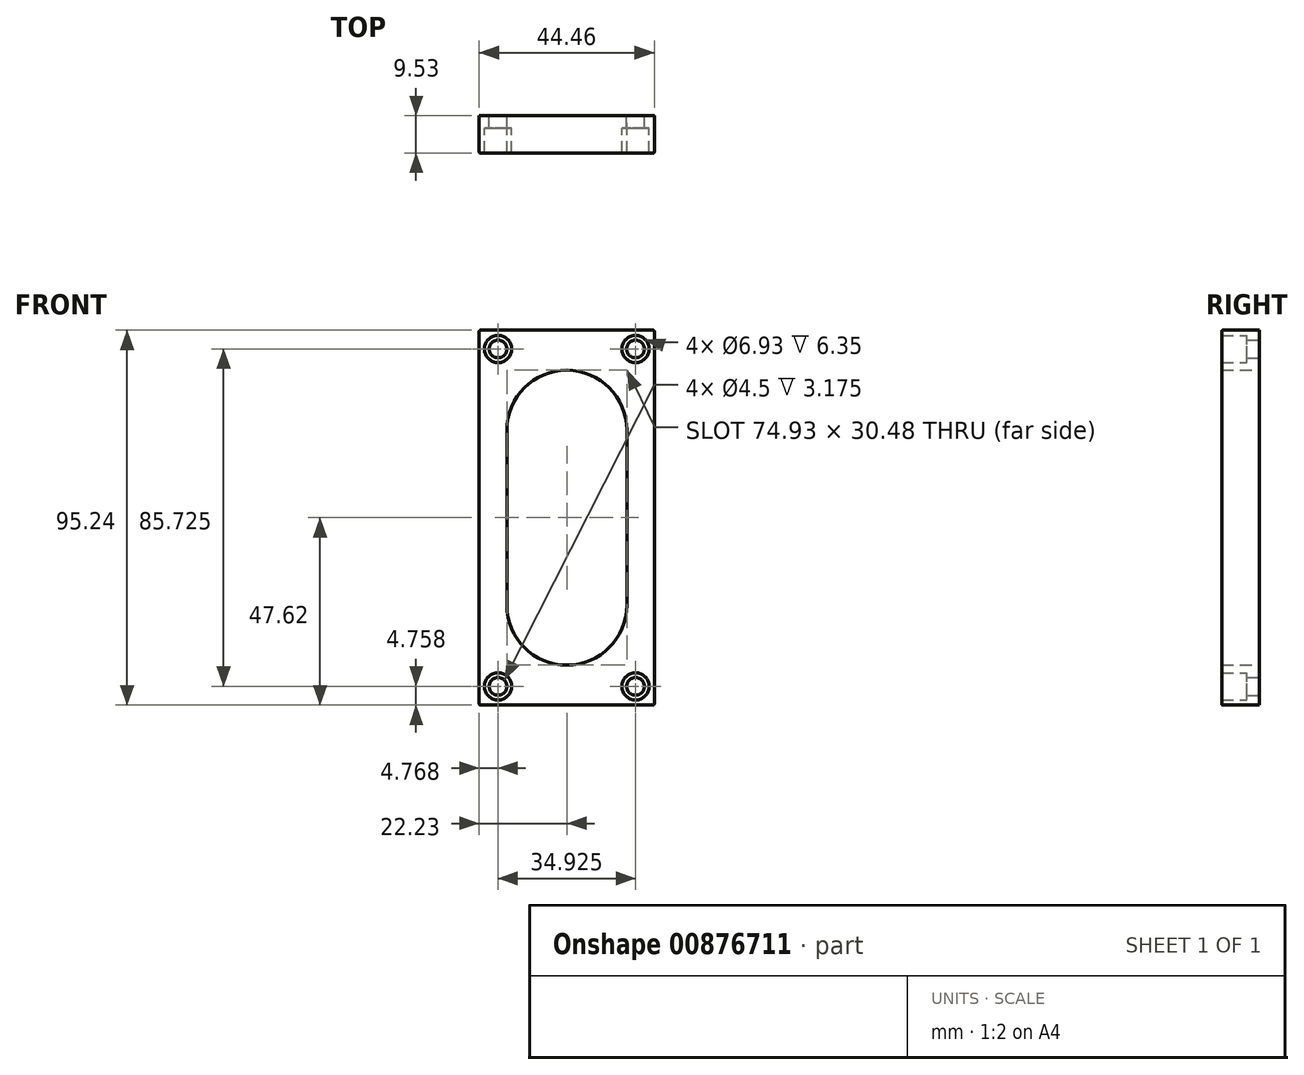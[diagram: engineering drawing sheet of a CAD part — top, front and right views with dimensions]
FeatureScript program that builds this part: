
annotation { "Feature Type Name" : "Feature", "Feature Type Description" : "" }
export const myFeature = defineFeature(function(context is Context, id is Id, definition is map)
    precondition{}
    {
        {
            var Q0;
            Q0=qCreatedBy(makeId("Front.planeOp"),FACE);
            var sketch = newSketch(context, id + "F0", { "sketchPlane" : qUnion([Q0])});
            skLineSegment(sketch, "E0.bottom", {"start": v(-22.23, 47.62) * mm, "end": v(22.23, 47.63) * mm});
            skLineSegment(sketch, "E0.top", {"start": v(-22.23, -47.63) * mm, "end": v(22.23, -47.62) * mm});
            skLineSegment(sketch, "E0.left", {"start": v(-22.23, 47.62) * mm, "end": v(-22.23, -47.63) * mm});
            skLineSegment(sketch, "E0.right", {"start": v(22.23, 47.63) * mm, "end": v(22.23, -47.62) * mm});
            skPoint(sketch, "E0.middle", {"position": v(0, 0) * mm});
            skPoint(sketch, "E1", {"position": v(17.46, 42.86) * mm});
            skPoint(sketch, "E2", {"position": v(-17.46, 42.86) * mm});
            skPoint(sketch, "E3", {"position": v(-17.46, -42.86) * mm});
            skPoint(sketch, "E4", {"position": v(17.46, -42.86) * mm});
            skCircle(sketch, "E5", {"center": v(-17.46, 42.86) * mm, "radius": 2.25 * mm});
            skCircle(sketch, "E6", {"center": v(17.46, 42.86) * mm, "radius": 2.25 * mm});
            skCircle(sketch, "E7", {"center": v(-17.46, -42.86) * mm, "radius": 2.25 * mm});
            skCircle(sketch, "E8", {"center": v(17.46, -42.86) * mm, "radius": 2.25 * mm});
            skPoint(sketch, "E9", {"position": v(0, 22.22) * mm});
            skPoint(sketch, "E10", {"position": v(0, -22.23) * mm});
            skArc(sketch, "E11", {"start": v(15.24, 22.22) * mm, "mid": v(0, 37.46) * mm, "end": v(-15.24, 22.22) * mm});
            skArc(sketch, "E12", {"start": v(15.24, -22.23) * mm, "mid": v(0, -37.47) * mm, "end": v(-15.24, -22.23) * mm});
            skLineSegment(sketch, "E13", {"start": v(-15.24, 22.23) * mm, "end": v(-15.24, -22.23) * mm});
            skLineSegment(sketch, "E14", {"start": v(15.24, 22.23) * mm, "end": v(15.24, -22.23) * mm});
            skCircle(sketch, "E15", {"center": v(17.46, 42.86) * mm, "radius": 3.47 * mm});
            skCircle(sketch, "E16", {"center": v(-17.46, 42.86) * mm, "radius": 3.47 * mm});
            skCircle(sketch, "E17", {"center": v(-17.46, -42.86) * mm, "radius": 3.47 * mm});
            skCircle(sketch, "E18", {"center": v(17.46, -42.86) * mm, "radius": 3.47 * mm});
            skSolve(sketch);
        }
        {
            var Q0;
            Q0=makeQuery(id+"F0.imprint","IMPRINT",FACE,{"disambiguationData":[TD([[makeQuery(id+"F0.imprint","IMPRINT",EDGE,{"derivedFrom":sQuery(id+"F0.wireOp",EDGE,"E0.bottom")}),-1.0]])]});
            extrude(context, id + "F1", {"entities" : qUnion([Q0]), "depth" : 6.35 * mm, "offsetDistance" : 25.4 * mm});
        }
        {
            var Q0;
            Q0=makeQuery(id+"F0.imprint","IMPRINT",FACE,{"disambiguationData":[TD([[makeQuery(id+"F0.imprint","IMPRINT",EDGE,{"derivedFrom":sQuery(id+"F0.wireOp",EDGE,"E5")}),-1.0]])]});
            var Q1;
            Q1=makeQuery(id+"F1.opExtrude","CAP_FACE",FACE,{"disambiguationData":[OSD([sQuery(id+"F0.wireOp",EDGE,"E0.bottom"),sQuery(id+"F0.wireOp",EDGE,"E0.top"),sQuery(id+"F0.wireOp",EDGE,"E0.left"),sQuery(id+"F0.wireOp",EDGE,"E0.right"),sQuery(id+"F0.wireOp",EDGE,"Io0cpQO2-bUGj-gnOB-Pf5R-uj9x4bCYI6hA"),sQuery(id+"F0.wireOp",EDGE,"OTM3Zsup-l6oP-84zL-IoTW-idEYZ85Jwz1g"),sQuery(id+"F0.wireOp",EDGE,"elozxBaz-7fZY-7FUM-z8d5-uTKpSDElM3XI"),sQuery(id+"F0.wireOp",EDGE,"y5RKX8gG-4KhF-hvzF-SgTC-0WD5jAp1ag1g"),sQuery(id+"F0.wireOp",EDGE,"WGjQV0SR-MPxT-HpUc-DE3J-uErIBKCCvPaX"),sQuery(id+"F0.wireOp",EDGE,"RAE5f9Y1-HzND-qi8Q-8VLe-MD1MPtyTG40E"),sQuery(id+"F0.wireOp",EDGE,"pfFnIftZ-3KcA-ZeHm-uxBQ-FoNbKLFE5cLc"),sQuery(id+"F0.wireOp",EDGE,"ZCBChMC9-1hS0-OwaU-jSbm-hkL8Xbsg0HCI")])],"isStart":false});
            var Q2;
            Q2=makeQuery(id+"F0.imprint","IMPRINT",FACE,{"disambiguationData":[TD([[makeQuery(id+"F0.imprint","IMPRINT",EDGE,{"derivedFrom":sQuery(id+"F0.wireOp",EDGE,"E6")}),-1.0]])]});
            var Q3;
            Q3=makeQuery(id+"F0.imprint","IMPRINT",FACE,{"disambiguationData":[TD([[makeQuery(id+"F0.imprint","IMPRINT",EDGE,{"derivedFrom":sQuery(id+"F0.wireOp",EDGE,"E0.bottom")}),-1.0]])]});
            var Q4;
            Q4=makeQuery(id+"F0.imprint","IMPRINT",FACE,{"disambiguationData":[TD([[makeQuery(id+"F0.imprint","IMPRINT",EDGE,{"derivedFrom":sQuery(id+"F0.wireOp",EDGE,"E7")}),-1.0]])]});
            var Q5;
            Q5=makeQuery(id+"F0.imprint","IMPRINT",FACE,{"disambiguationData":[TD([[makeQuery(id+"F0.imprint","IMPRINT",EDGE,{"derivedFrom":sQuery(id+"F0.wireOp",EDGE,"E8")}),-1.0]])]});
            extrude(context, id + "F2", {"entities" : qUnion([Q0, Q1, Q2, Q3, Q4, Q5]), "operationType" : NewBodyOperationType.ADD, "depth" : 3.17 * mm, "offsetDistance" : 25.4 * mm});
        }
        {
            var Q0;
            {var subQ0=sQuery(id+"F0.wireOp",EDGE,"E0.left");Q0=makeQuery(id+"F2.opExtrude","CAP_EDGE",EDGE,{"disambiguationData":[OSD([subQ0]),TDD([makeQuery(id+"F1.opExtrude","CAP_EDGE",EDGE,{"disambiguationData":[OSD([subQ0])],"isStart":false})])],"isStart":false});}
            var Q1;
            {var subQ0=sQuery(id+"F0.wireOp",EDGE,"E0.top");Q1=makeQuery(id+"F2.opExtrude","CAP_EDGE",EDGE,{"disambiguationData":[OSD([subQ0]),TDD([makeQuery(id+"F1.opExtrude","CAP_EDGE",EDGE,{"disambiguationData":[OSD([subQ0])],"isStart":false})])],"isStart":false});}
            var Q2;
            {var subQ0=sQuery(id+"F0.wireOp",EDGE,"E0.right");Q2=makeQuery(id+"F2.opExtrude","CAP_EDGE",EDGE,{"disambiguationData":[OSD([subQ0]),TDD([makeQuery(id+"F1.opExtrude","CAP_EDGE",EDGE,{"disambiguationData":[OSD([subQ0])],"isStart":false})])],"isStart":false});}
            var Q3;
            {var subQ0=sQuery(id+"F0.wireOp",EDGE,"E0.bottom");Q3=makeQuery(id+"F2.opExtrude","CAP_EDGE",EDGE,{"disambiguationData":[OSD([subQ0]),TDD([makeQuery(id+"F1.opExtrude","CAP_EDGE",EDGE,{"disambiguationData":[OSD([subQ0])],"isStart":false})])],"isStart":false});}
            var Q4;
            {var subQ0=sQuery(id+"F0.wireOp",EDGE,"E0.left");var subQ1=sQuery(id+"F0.wireOp",EDGE,"E0.bottom");Q4=makeQuery(id+"F2.boolean.opBoolean","MERGE",EDGE,{"derivedFrom":[makeQuery(id+"F1.opExtrude","SWEPT_EDGE",EDGE,{"disambiguationData":[OSD([subQ1,subQ0])]}),makeQuery(id+"F2.opExtrude","SWEPT_EDGE",EDGE,{"disambiguationData":[OSD([subQ1,subQ0]),TDD([makeQuery(id+"F0.imprint","INTERSECT",VERTEX,{"derivedFrom":[subQ1,subQ0]})])]}),makeQuery(id+"F2.opExtrude","SWEPT_EDGE",EDGE,{"disambiguationData":[OSD([subQ1,subQ0]),TDD([makeQuery(id+"F1.opExtrude","CAP_VERTEX",VERTEX,{"disambiguationData":[OSD([subQ1,subQ0])],"isStart":false})])]})]});}
            var Q5;
            {var subQ0=sQuery(id+"F0.wireOp",EDGE,"E0.right");var subQ1=sQuery(id+"F0.wireOp",EDGE,"E0.bottom");Q5=makeQuery(id+"F2.boolean.opBoolean","MERGE",EDGE,{"derivedFrom":[makeQuery(id+"F1.opExtrude","SWEPT_EDGE",EDGE,{"disambiguationData":[OSD([subQ1,subQ0])]}),makeQuery(id+"F2.opExtrude","SWEPT_EDGE",EDGE,{"disambiguationData":[OSD([subQ1,subQ0]),TDD([makeQuery(id+"F0.imprint","INTERSECT",VERTEX,{"derivedFrom":[subQ1,subQ0]})])]}),makeQuery(id+"F2.opExtrude","SWEPT_EDGE",EDGE,{"disambiguationData":[OSD([subQ1,subQ0]),TDD([makeQuery(id+"F1.opExtrude","CAP_VERTEX",VERTEX,{"disambiguationData":[OSD([subQ1,subQ0])],"isStart":false})])]})]});}
            var Q6;
            {var subQ0=sQuery(id+"F0.wireOp",EDGE,"E0.right");var subQ1=sQuery(id+"F0.wireOp",EDGE,"E0.top");Q6=makeQuery(id+"F2.boolean.opBoolean","MERGE",EDGE,{"derivedFrom":[makeQuery(id+"F1.opExtrude","SWEPT_EDGE",EDGE,{"disambiguationData":[OSD([subQ1,subQ0])]}),makeQuery(id+"F2.opExtrude","SWEPT_EDGE",EDGE,{"disambiguationData":[OSD([subQ1,subQ0]),TDD([makeQuery(id+"F0.imprint","INTERSECT",VERTEX,{"derivedFrom":[subQ1,subQ0]})])]}),makeQuery(id+"F2.opExtrude","SWEPT_EDGE",EDGE,{"disambiguationData":[OSD([subQ1,subQ0]),TDD([makeQuery(id+"F1.opExtrude","CAP_VERTEX",VERTEX,{"disambiguationData":[OSD([subQ1,subQ0])],"isStart":false})])]})]});}
            var Q7;
            {var subQ0=sQuery(id+"F0.wireOp",EDGE,"E0.left");var subQ1=sQuery(id+"F0.wireOp",EDGE,"E0.top");Q7=makeQuery(id+"F2.boolean.opBoolean","MERGE",EDGE,{"derivedFrom":[makeQuery(id+"F1.opExtrude","SWEPT_EDGE",EDGE,{"disambiguationData":[OSD([subQ1,subQ0])]}),makeQuery(id+"F2.opExtrude","SWEPT_EDGE",EDGE,{"disambiguationData":[OSD([subQ1,subQ0]),TDD([makeQuery(id+"F0.imprint","INTERSECT",VERTEX,{"derivedFrom":[subQ1,subQ0]})])]}),makeQuery(id+"F2.opExtrude","SWEPT_EDGE",EDGE,{"disambiguationData":[OSD([subQ1,subQ0]),TDD([makeQuery(id+"F1.opExtrude","CAP_VERTEX",VERTEX,{"disambiguationData":[OSD([subQ1,subQ0])],"isStart":false})])]})]});}
            var Q8;
            Q8=makeQuery(id+"F2.opExtrude","CAP_EDGE",EDGE,{"disambiguationData":[OSD([sQuery(id+"F0.wireOp",EDGE,"y5RKX8gG-4KhF-hvzF-SgTC-0WD5jAp1ag1g")])],"isStart":false});
            var Q9;
            Q9=makeQuery(id+"F2.opExtrude","CAP_EDGE",EDGE,{"disambiguationData":[OSD([sQuery(id+"F0.wireOp",EDGE,"elozxBaz-7fZY-7FUM-z8d5-uTKpSDElM3XI")])],"isStart":false});
            var Q10;
            Q10=makeQuery(id+"F2.opExtrude","CAP_EDGE",EDGE,{"disambiguationData":[OSD([sQuery(id+"F0.wireOp",EDGE,"Io0cpQO2-bUGj-gnOB-Pf5R-uj9x4bCYI6hA")])],"isStart":false});
            var Q11;
            Q11=makeQuery(id+"F2.opExtrude","CAP_EDGE",EDGE,{"disambiguationData":[OSD([sQuery(id+"F0.wireOp",EDGE,"OTM3Zsup-l6oP-84zL-IoTW-idEYZ85Jwz1g")])],"isStart":false});
            var Q12;
            {var subQ0=sQuery(id+"F0.wireOp",EDGE,"WGjQV0SR-MPxT-HpUc-DE3J-uErIBKCCvPaX");Q12=makeQuery(id+"F2.opExtrude","CAP_EDGE",EDGE,{"disambiguationData":[OSD([subQ0]),TDD([makeQuery(id+"F1.opExtrude","CAP_EDGE",EDGE,{"disambiguationData":[OSD([subQ0])],"isStart":false})])],"isStart":false});}
            var Q13;
            {var subQ0=sQuery(id+"F0.wireOp",EDGE,"ZCBChMC9-1hS0-OwaU-jSbm-hkL8Xbsg0HCI");Q13=makeQuery(id+"F2.opExtrude","CAP_EDGE",EDGE,{"disambiguationData":[OSD([subQ0]),TDD([makeQuery(id+"F1.opExtrude","CAP_EDGE",EDGE,{"disambiguationData":[OSD([subQ0])],"isStart":false})])],"isStart":false});}
            var Q14;
            {var subQ0=sQuery(id+"F0.wireOp",EDGE,"RAE5f9Y1-HzND-qi8Q-8VLe-MD1MPtyTG40E");Q14=makeQuery(id+"F2.opExtrude","CAP_EDGE",EDGE,{"disambiguationData":[OSD([subQ0]),TDD([makeQuery(id+"F1.opExtrude","CAP_EDGE",EDGE,{"disambiguationData":[OSD([subQ0])],"isStart":false})])],"isStart":false});}
            var Q15;
            {var subQ0=sQuery(id+"F0.wireOp",EDGE,"pfFnIftZ-3KcA-ZeHm-uxBQ-FoNbKLFE5cLc");Q15=makeQuery(id+"F2.opExtrude","CAP_EDGE",EDGE,{"disambiguationData":[OSD([subQ0]),TDD([makeQuery(id+"F1.opExtrude","CAP_EDGE",EDGE,{"disambiguationData":[OSD([subQ0])],"isStart":false})])],"isStart":false});}
            fillet(context, id + "F3", {"entities" : qUnion([Q0, Q1, Q2, Q3, Q4, Q5, Q6, Q7, Q8, Q9, Q10, Q11, Q12, Q13, Q14, Q15]), "radius" : 0.25 * mm, "tangentPropagation" : true, "allowEdgeOverflow" : false});
        }
    });
